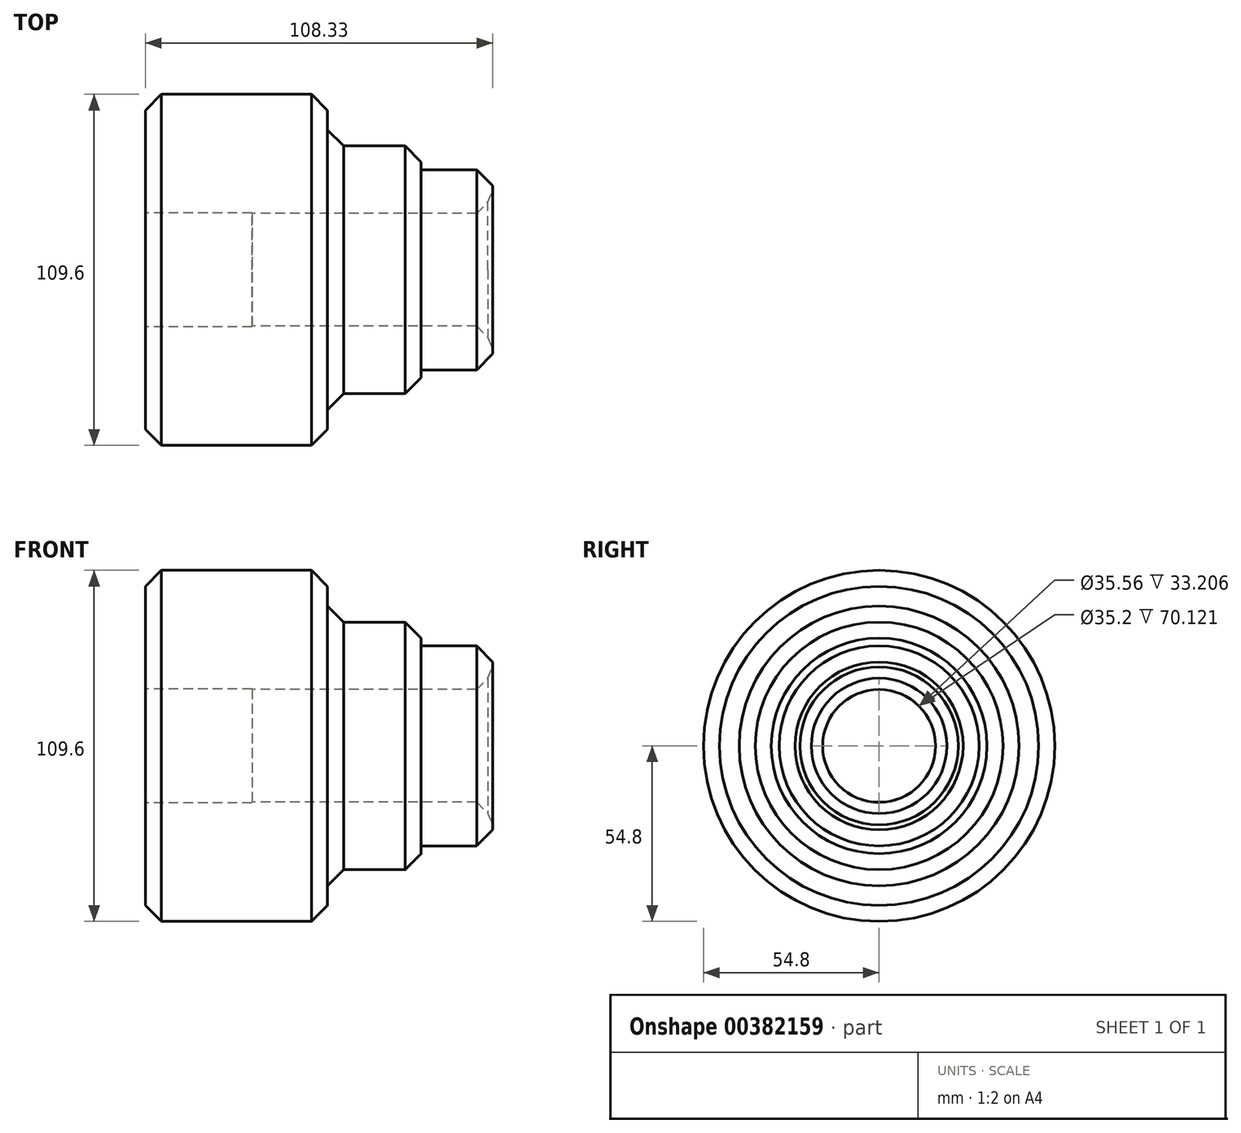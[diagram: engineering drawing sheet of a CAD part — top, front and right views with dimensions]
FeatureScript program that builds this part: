
annotation { "Feature Type Name" : "Feature", "Feature Type Description" : "" }
export const myFeature = defineFeature(function(context is Context, id is Id, definition is map)
    precondition{}
    {
        {
            var Q0;
            Q0=qCreatedBy(makeId("Front.planeOp"),FACE);
            var sketch = newSketch(context, id + "F0", { "sketchPlane" : qUnion([Q0])});
            skLineSegment(sketch, "E0", {"start": v(-64.42, 0) * mm, "end": v(64.96, 0) * mm, "construction": true});
            skSolve(sketch);
        }
        {
            var Q0;
            Q0=qCreatedBy(makeId("Front.planeOp"),FACE);
            var sketch = newSketch(context, id + "F1", { "sketchPlane" : qUnion([Q0])});
            skLineSegment(sketch, "E1.bottom", {"start": v(-70.77, 54.8) * mm, "end": v(-13.97, 54.8) * mm});
            skLineSegment(sketch, "E1.top", {"start": v(-70.77, 17.78) * mm, "end": v(-13.97, 17.78) * mm});
            skLineSegment(sketch, "E1.left", {"start": v(-70.77, 54.8) * mm, "end": v(-70.77, 17.78) * mm});
            skLineSegment(sketch, "E1.right", {"start": v(-13.97, 54.8) * mm, "end": v(-13.97, 17.78) * mm});
            skLineSegment(sketch, "E2.bottom", {"start": v(-37.56, 38.65) * mm, "end": v(15.24, 38.65) * mm});
            skLineSegment(sketch, "E2.top", {"start": v(-37.56, 17.6) * mm, "end": v(15.24, 17.6) * mm});
            skLineSegment(sketch, "E2.left", {"start": v(-37.56, 38.65) * mm, "end": v(-37.56, 17.6) * mm});
            skLineSegment(sketch, "E2.right", {"start": v(15.24, 38.65) * mm, "end": v(15.24, 17.6) * mm});
            skLineSegment(sketch, "E3.bottom", {"start": v(-4, 31.2) * mm, "end": v(37.56, 31.2) * mm});
            skLineSegment(sketch, "E3.top", {"start": v(-4, 17.6) * mm, "end": v(37.56, 17.6) * mm});
            skLineSegment(sketch, "E3.left", {"start": v(-4, 31.2) * mm, "end": v(-4, 17.6) * mm});
            skLineSegment(sketch, "E3.right", {"start": v(37.56, 31.2) * mm, "end": v(37.56, 17.6) * mm});
            skSolve(sketch);
        }
        {
            var Q0;
            Q0 = qSketchRegion(id + "F1", true);
            var Q1;
            Q1=sQuery(id+"F0.wireOp",EDGE,"E0");
            revolve(context, id + "F2", {"entities" : qUnion([Q0]), "axis" : qUnion([Q1]), "revolveType" : RevolveType.FULL});
        }
        {
            var Q0;
            Q0=makeQuery(id+"F2.opRevolve","SWEPT_FACE",FACE,{"disambiguationData":[OSD([sQuery(id+"F1.wireOp",EDGE,"E1.bottom")])]});
            var Q1;
            Q1=makeQuery(id+"F2.opRevolve","SWEPT_EDGE",EDGE,{"disambiguationData":[OSD([sQuery(id+"F1.wireOp",EDGE,"E3.top"),sQuery(id+"F1.wireOp",EDGE,"E3.right")])]});
            chamfer(context, id + "F3", {"entities" : qUnion([Q0, Q1]), "width" : 5 * mm, "tangentPropagation" : true});
        }
        {
            var Q0;
            Q0=makeQuery(id+"F2.opRevolve","SWEPT_EDGE",EDGE,{"disambiguationData":[OSD([sQuery(id+"F1.wireOp",EDGE,"E3.bottom"),sQuery(id+"F1.wireOp",EDGE,"E3.right")])]});
            var Q1;
            {var subQ0=sQuery(id+"F1.wireOp",EDGE,"E3.right");Q1=makeQuery(id+"F3.opChamfer","BLEND_EDGE",EDGE,{"blendedFrom":[makeQuery(id+"F2.opRevolve","SWEPT_EDGE",EDGE,{"disambiguationData":[OSD([sQuery(id+"F1.wireOp",EDGE,"E3.top"),subQ0])]}),makeQuery(id+"F2.opRevolve","SWEPT_FACE",FACE,{"disambiguationData":[OSD([subQ0])]})],"blendedInto":[makeQuery(id+"F2.opRevolve","SWEPT_FACE",FACE,{"disambiguationData":[OSD([subQ0])]})]});}
            var Q2;
            Q2=makeQuery(id+"F2.opRevolve","SWEPT_EDGE",EDGE,{"disambiguationData":[OSD([sQuery(id+"F1.wireOp",EDGE,"E2.bottom"),sQuery(id+"F1.wireOp",EDGE,"E2.right")])]});
            var Q3;
            Q3=makeQuery(id+"F2.opRevolve","SWEPT_FACE",FACE,{"disambiguationData":[OSD([sQuery(id+"F1.wireOp",EDGE,"E2.bottom")])]});
            chamfer(context, id + "F4", {"entities" : qUnion([Q0, Q1, Q2, Q3]), "width" : 5 * mm, "tangentPropagation" : true});
        }
    });
